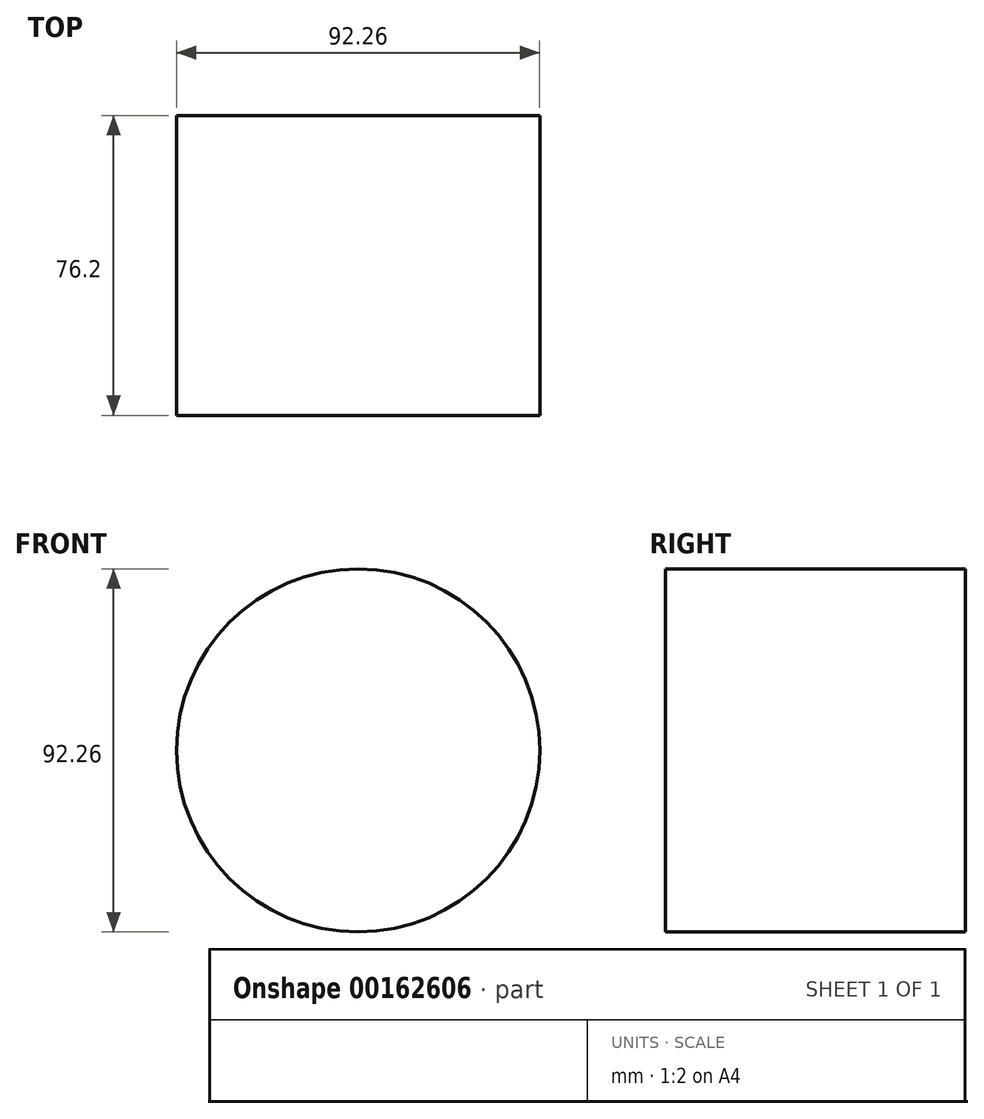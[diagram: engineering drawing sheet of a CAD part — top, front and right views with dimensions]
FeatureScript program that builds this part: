
annotation { "Feature Type Name" : "Feature", "Feature Type Description" : "" }
export const myFeature = defineFeature(function(context is Context, id is Id, definition is map)
    precondition{}
    {
        {
            var Q0;
            Q0=qCreatedBy(makeId("Front.planeOp"),FACE);
            var sketch = newSketch(context, id + "F0", { "sketchPlane" : qUnion([Q0])});
            skCircle(sketch, "E0", {"center": v(0, 0) * mm, "radius": 46.13 * mm});
            skSolve(sketch);
        }
        {
            var Q0;
            Q0=makeQuery(id+"F0.imprint","IMPRINT",FACE,{"disambiguationData":[TD([[makeQuery(id+"F0.imprint","IMPRINT",EDGE,{"derivedFrom":sQuery(id+"F0.wireOp",EDGE,"E0")}),1.0]])]});
            extrude(context, id + "F1", {"entities" : qUnion([Q0]), "depth" : 76.2 * mm});
        }
    });
